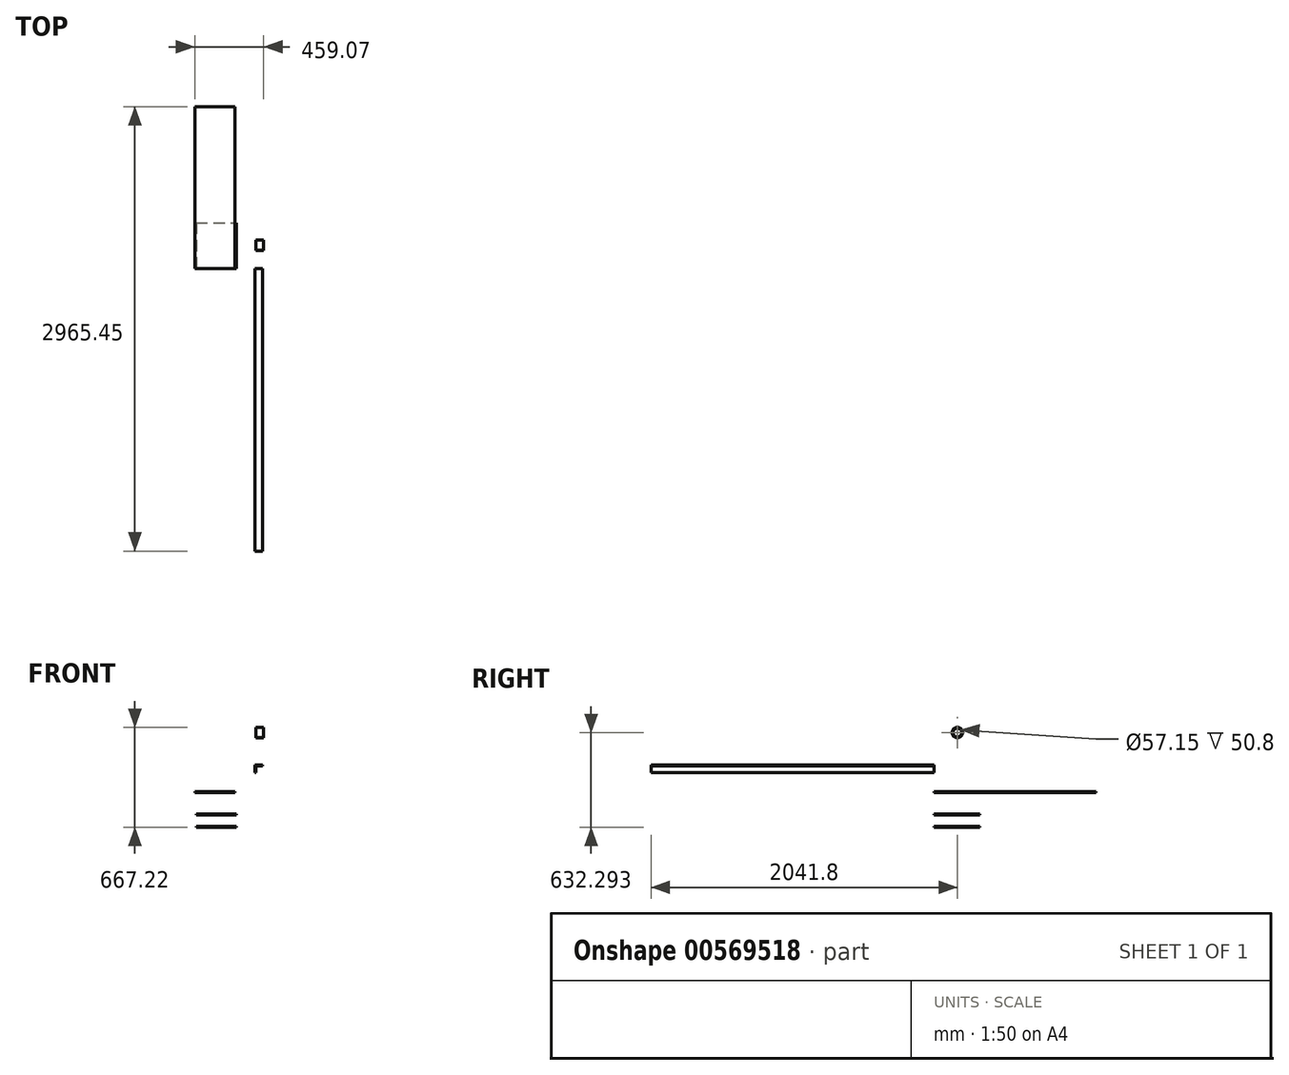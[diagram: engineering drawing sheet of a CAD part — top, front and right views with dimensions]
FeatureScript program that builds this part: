
annotation { "Feature Type Name" : "Feature", "Feature Type Description" : "" }
export const myFeature = defineFeature(function(context is Context, id is Id, definition is map)
    precondition{}
    {
        {
            var Q0;
            Q0=qCreatedBy(makeId("Front.planeOp"),FACE);
            var sketch = newSketch(context, id + "F0", { "sketchPlane" : qUnion([Q0])});
            skLineSegment(sketch, "E0.bottom", {"start": v(-7.25, -21.1) * mm, "end": v(-0.9, -21.1) * mm});
            skLineSegment(sketch, "E0.top", {"start": v(-7.25, 29.7) * mm, "end": v(-0.9, 29.7) * mm});
            skLineSegment(sketch, "E0.left", {"start": v(-7.25, -21.1) * mm, "end": v(-7.25, 29.7) * mm});
            skLineSegment(sketch, "E0.right", {"start": v(-0.9, -21.1) * mm, "end": v(-0.9, 29.7) * mm});
            skLineSegment(sketch, "E1.bottom", {"start": v(-0.9, 29.7) * mm, "end": v(43.55, 29.7) * mm});
            skLineSegment(sketch, "E1.top", {"start": v(-0.9, 23.36) * mm, "end": v(43.55, 23.36) * mm});
            skLineSegment(sketch, "E1.left", {"start": v(-0.9, 29.7) * mm, "end": v(-0.9, 23.36) * mm});
            skLineSegment(sketch, "E1.right", {"start": v(43.55, 29.7) * mm, "end": v(43.55, 23.36) * mm});
            skSolve(sketch);
        }
        {
            var Q0;
            Q0=makeQuery(id+"F0.imprint","IMPRINT",FACE,{"disambiguationData":[TD([[makeQuery(id+"F0.imprint","IMPRINT",EDGE,{"derivedFrom":sQuery(id+"F0.wireOp",EDGE,"E0.bottom")}),1.0]])]});
            var Q1;
            Q1=makeQuery(id+"F0.imprint","IMPRINT",FACE,{"disambiguationData":[TD([[makeQuery(id+"F0.imprint","IMPRINT",EDGE,{"derivedFrom":sQuery(id+"F0.wireOp",EDGE,"E1.bottom")}),-1.0]])]});
            extrude(context, id + "F1", {"entities" : qUnion([Q0, Q1]), "depth" : 1885.95 * mm, "offsetDistance" : 25.4 * mm});
        }
        {
            var Q0;
            Q0=qCreatedBy(makeId("Right.planeOp"),FACE);
            var sketch = newSketch(context, id + "F2", { "sketchPlane" : qUnion([Q0])});
            skCircle(sketch, "E2", {"center": v(155.85, 246.94) * mm, "radius": 34.93 * mm});
            skCircle(sketch, "E3", {"center": v(155.85, 246.94) * mm, "radius": 28.58 * mm});
            skSolve(sketch);
        }
        {
            var Q0;
            Q0=makeQuery(id+"F2.imprint","IMPRINT",FACE,{"disambiguationData":[TD([[makeQuery(id+"F2.imprint","IMPRINT",EDGE,{"derivedFrom":sQuery(id+"F2.wireOp",EDGE,"E2")}),1.0]])]});
            extrude(context, id + "F3", {"entities" : qUnion([Q0]), "depth" : 50.8 * mm, "offsetDistance" : 25.4 * mm});
        }
        {
            var Q0;
            Q0=qCreatedBy(makeId("Front.planeOp"),FACE);
            var sketch = newSketch(context, id + "F4", { "sketchPlane" : qUnion([Q0])});
            skLineSegment(sketch, "E4.bottom", {"start": v(-408.27, -153.27) * mm, "end": v(-141.57, -153.27) * mm});
            skLineSegment(sketch, "E4.top", {"start": v(-408.27, -146.92) * mm, "end": v(-141.57, -146.92) * mm});
            skLineSegment(sketch, "E4.left", {"start": v(-408.27, -153.27) * mm, "end": v(-408.27, -146.92) * mm});
            skLineSegment(sketch, "E4.right", {"start": v(-141.57, -153.27) * mm, "end": v(-141.57, -146.92) * mm});
            skLineSegment(sketch, "E5.bottom", {"start": v(-408.27, -146.92) * mm, "end": v(-401.92, -146.92) * mm});
            skLineSegment(sketch, "E5.top", {"start": v(-408.27, -70.72) * mm, "end": v(-401.92, -70.72) * mm});
            skLineSegment(sketch, "E5.left", {"start": v(-408.27, -146.92) * mm, "end": v(-408.27, -70.72) * mm});
            skLineSegment(sketch, "E5.right", {"start": v(-401.92, -146.92) * mm, "end": v(-401.92, -70.72) * mm});
            skLineSegment(sketch, "E6.bottom", {"start": v(-141.57, -146.92) * mm, "end": v(-147.92, -146.92) * mm});
            skLineSegment(sketch, "E6.top", {"start": v(-141.57, -70.72) * mm, "end": v(-147.92, -70.72) * mm});
            skLineSegment(sketch, "E6.left", {"start": v(-141.57, -146.92) * mm, "end": v(-141.57, -70.72) * mm});
            skLineSegment(sketch, "E6.right", {"start": v(-147.92, -146.92) * mm, "end": v(-147.92, -70.72) * mm});
            skSolve(sketch);
        }
        {
            var Q0;
            Q0=makeQuery(id+"F4.imprint","IMPRINT",FACE,{"disambiguationData":[TD([[makeQuery(id+"F4.imprint","IMPRINT",EDGE,{"derivedFrom":sQuery(id+"F4.wireOp",EDGE,"E5.bottom")}),1.0]])]});
            var Q1;
            Q1=makeQuery(id+"F4.imprint","IMPRINT",FACE,{"disambiguationData":[TD([[makeQuery(id+"F4.imprint","IMPRINT",EDGE,{"derivedFrom":sQuery(id+"F4.wireOp",EDGE,"E6.bottom")}),-1.0]])]});
            var Q2;
            Q2=makeQuery(id+"F4.imprint","IMPRINT",FACE,{"disambiguationData":[TD([[makeQuery(id+"F4.imprint","IMPRINT",EDGE,{"derivedFrom":sQuery(id+"F4.wireOp",EDGE,"E4.bottom")}),1.0]])]});
            extrude(context, id + "F5", {"entities" : qUnion([Q0, Q1, Q2]), "oppositeDirection" : true, "depth" : 1079.5 * mm, "offsetDistance" : 25.4 * mm});
        }
        {
            var Q0;
            Q0=qCreatedBy(makeId("Front.planeOp"),FACE);
            var sketch = newSketch(context, id + "F6", { "sketchPlane" : qUnion([Q0])});
            skLineSegment(sketch, "E7.bottom", {"start": v(-398.53, -385.35) * mm, "end": v(-131.83, -385.35) * mm});
            skLineSegment(sketch, "E7.top", {"start": v(-398.53, -379) * mm, "end": v(-131.83, -379) * mm});
            skLineSegment(sketch, "E7.left", {"start": v(-398.53, -385.35) * mm, "end": v(-398.53, -379) * mm});
            skLineSegment(sketch, "E7.right", {"start": v(-131.83, -385.35) * mm, "end": v(-131.83, -379) * mm});
            skLineSegment(sketch, "E8.bottom", {"start": v(-398.53, -379) * mm, "end": v(-392.18, -379) * mm});
            skLineSegment(sketch, "E8.top", {"start": v(-398.53, -302.8) * mm, "end": v(-392.18, -302.8) * mm});
            skLineSegment(sketch, "E8.left", {"start": v(-398.53, -379) * mm, "end": v(-398.53, -302.8) * mm});
            skLineSegment(sketch, "E8.right", {"start": v(-392.18, -379) * mm, "end": v(-392.18, -302.8) * mm});
            skLineSegment(sketch, "E9.bottom", {"start": v(-131.83, -379) * mm, "end": v(-138.18, -379) * mm});
            skLineSegment(sketch, "E9.top", {"start": v(-131.83, -302.8) * mm, "end": v(-138.18, -302.8) * mm});
            skLineSegment(sketch, "E9.left", {"start": v(-131.83, -379) * mm, "end": v(-131.83, -302.8) * mm});
            skLineSegment(sketch, "E9.right", {"start": v(-138.18, -379) * mm, "end": v(-138.18, -302.8) * mm});
            skLineSegment(sketch, "E10.bottom", {"start": v(-398.53, -302.8) * mm, "end": v(-131.63, -302.8) * mm});
            skLineSegment(sketch, "E10.top", {"start": v(-398.53, -296.45) * mm, "end": v(-131.63, -296.45) * mm});
            skLineSegment(sketch, "E10.left", {"start": v(-398.53, -302.8) * mm, "end": v(-398.53, -296.45) * mm});
            skLineSegment(sketch, "E10.right", {"start": v(-131.63, -302.8) * mm, "end": v(-131.63, -296.45) * mm});
            skSolve(sketch);
        }
        {
            var Q0;
            Q0=makeQuery(id+"F6.imprint","IMPRINT",FACE,{"disambiguationData":[TD([[makeQuery(id+"F6.imprint","IMPRINT",EDGE,{"derivedFrom":sQuery(id+"F6.wireOp",EDGE,"E10.top")}),-1.0]])]});
            var Q1;
            Q1=makeQuery(id+"F6.imprint","IMPRINT",FACE,{"disambiguationData":[TD([[makeQuery(id+"F6.imprint","IMPRINT",EDGE,{"derivedFrom":sQuery(id+"F6.wireOp",EDGE,"E8.bottom")}),1.0]])]});
            var Q2;
            Q2=makeQuery(id+"F6.imprint","IMPRINT",FACE,{"disambiguationData":[TD([[makeQuery(id+"F6.imprint","IMPRINT",EDGE,{"derivedFrom":sQuery(id+"F6.wireOp",EDGE,"E7.bottom")}),1.0]])]});
            var Q3;
            Q3=makeQuery(id+"F6.imprint","IMPRINT",FACE,{"disambiguationData":[TD([[makeQuery(id+"F6.imprint","IMPRINT",EDGE,{"derivedFrom":sQuery(id+"F6.wireOp",EDGE,"E9.bottom")}),-1.0]])]});
            extrude(context, id + "F7", {"entities" : qUnion([Q0, Q1, Q2, Q3]), "oppositeDirection" : true, "depth" : 304.8 * mm, "offsetDistance" : 25.4 * mm});
        }
    });
